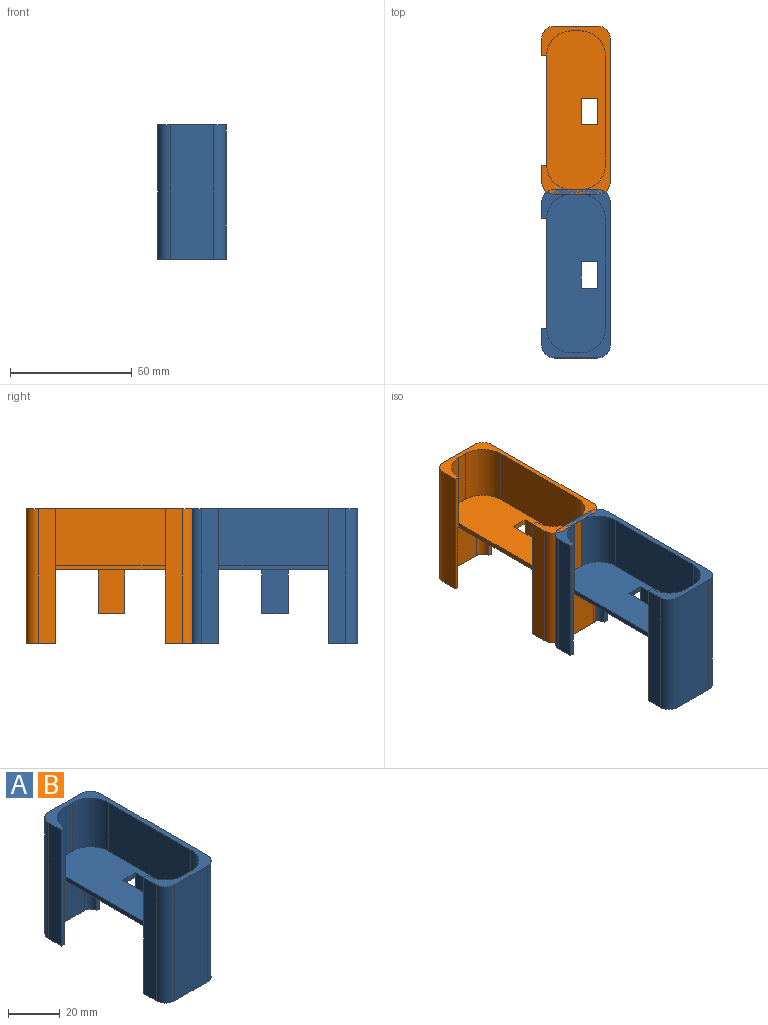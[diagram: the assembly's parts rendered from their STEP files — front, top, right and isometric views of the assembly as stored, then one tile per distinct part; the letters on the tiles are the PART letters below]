
ASSEMBLY  parts=2 mates=1
PART A: 42 faces, bbox 28x69x55 mm
  f0: plane 66x26.5mm, normal (0,0,-1), area 1607.6mm2, adj f7,f19,f20,f21,f23,f24,f25,f26
  f1: plane 69x28mm, normal (0,0,1), area 346.4mm2, adj f2,f4,f5,f6,f7,f8,f9,f10
  f2: plane 55x7mm, normal (-1,0,0), area 385mm2, adj f1,f11,f25,f35
  f3: plane 65x24mm, normal (0,0,1), area 1398.3mm2, adj f8,f9,f10,f15,f16,f17,f18,f19
  f4: plane 55x18mm, normal (0,1,0), area 990mm2, adj f1,f11,f14,f35
  f5: plane 55x7mm, normal (-1,0,0), area 385mm2, adj f1,f12,f23,f41
  f6: plane 55x18mm, normal (0,-1,0), area 990mm2, adj f1,f12,f13,f41
  f7: plane 59x25mm, normal (1,0,0), area 1475mm2, adj f0,f1,f13,f14
  f8: plane 23x4mm, normal (0,-1,0), area 92mm2, adj f1,f3,f16,f18
  f9: plane 23x4mm, normal (0,1,0), area 92mm2, adj f1,f3,f15,f17
  f10: plane 45x23mm, normal (-1,0,0), area 1035mm2, adj f1,f3,f15,f16
  f11: cylinder r=5mm len=55mm, axis (0,0,-1), area 432mm2, adj f1,f2,f4,f35
  f12: cylinder r=5mm len=55mm, axis (0,0,1), area 432mm2, adj f1,f5,f6,f41
  f13: cylinder r=5mm len=55mm, axis (0,0,-1), area 432mm2, adj f1,f6,f7,f36,f41
  f14: cylinder r=5mm len=55mm, axis (0,0,1), area 432mm2, adj f1,f4,f7,f30,f35
  f15: cylinder r=10mm len=23mm, axis (0,0,1), area 361.3mm2, adj f1,f3,f9,f10
  f16: cylinder r=10mm len=23mm, axis (0,0,-1), area 361.3mm2, adj f1,f3,f8,f10
  f17: cylinder r=10mm len=23mm, axis (0,0,-1), area 361.3mm2, adj f1,f3,f9,f23
  f18: cylinder r=10mm len=23mm, axis (0,0,1), area 361.3mm2, adj f1,f3,f8,f25
  f19: plane 6.9x2mm, normal (0,-1,0), area 13.8mm2, adj f0,f3,f20,f22
  f20: plane 11x2mm, normal (1,0,0), area 22mm2, adj f0,f3,f19,f21
  f21: plane 6.9x2mm, normal (0,1,0), area 13.8mm2, adj f0,f3,f20,f22
  f22: plane 20x11mm, normal (-1,0,0), area 220mm2, adj f3,f19,f21,f26,f27,f29
  f23: plane 55x2mm, normal (0,1,0), area 95mm2, adj f0,f1,f5,f17,f24,f37,f41
  f24: plane 45x2mm, normal (-1,0,0), area 90mm2, adj f0,f3,f23,f25
  f25: plane 55x2mm, normal (0,-1,0), area 95mm2, adj f0,f1,f2,f18,f24,f34,f35
  f26: plane 18x2mm, normal (0,-1,0), area 36mm2, adj f0,f22,f28,f29
  f27: plane 18x2mm, normal (0,1,0), area 36mm2, adj f0,f22,f28,f29
  f28: plane 18x11mm, normal (1,0,0), area 198mm2, adj f0,f26,f27,f29
  f29: plane 11x2mm, normal (0,0,-1), area 22mm2, adj f22,f26,f27,f28
  f30: plane 30x1.5mm, normal (0,-1,0), area 45mm2, adj f0,f14,f31,f35
  f31: cylinder r=3.5mm len=30mm, axis (0,0,1), area 164.9mm2, adj f0,f30,f32,f35
  f32: plane 30x18mm, normal (0,-1,0), area 540mm2, adj f0,f31,f33,f35
  f33: cylinder r=3.5mm len=30mm, axis (0,0,1), area 164.9mm2, adj f0,f32,f34,f35
  f34: plane 30x7mm, normal (1,0,0), area 210mm2, adj f0,f25,f33,f35
  f35: plane 28x12mm, normal (0,0,-1), area 57.5mm2, adj f2,f4,f11,f14,f25,f30,f31,f32
  f36: plane 30x1.5mm, normal (0,1,0), area 45mm2, adj f0,f13,f40,f41
  f37: plane 30x7mm, normal (1,0,0), area 210mm2, adj f0,f23,f38,f41
  f38: cylinder r=3.5mm len=30mm, axis (0,0,1), area 164.9mm2, adj f0,f37,f39,f41
  f39: plane 30x18mm, normal (0,1,0), area 540mm2, adj f0,f38,f40,f41
  f40: cylinder r=3.5mm len=30mm, axis (0,0,1), area 164.9mm2, adj f0,f36,f39,f41
  f41: plane 28x12mm, normal (0,0,-1), area 57.5mm2, adj f5,f6,f12,f13,f23,f36,f37,f38
PART B: same geometry as A
PLACE A t=(46.69,-69.37,-7.88)mm
PLACE B t=(46.69,-2.37,-7.88)mm
MATE fastened A.f8 <-> B.f6  axis (0,-1,0) through (32.55,-33.58,17.12)mm
